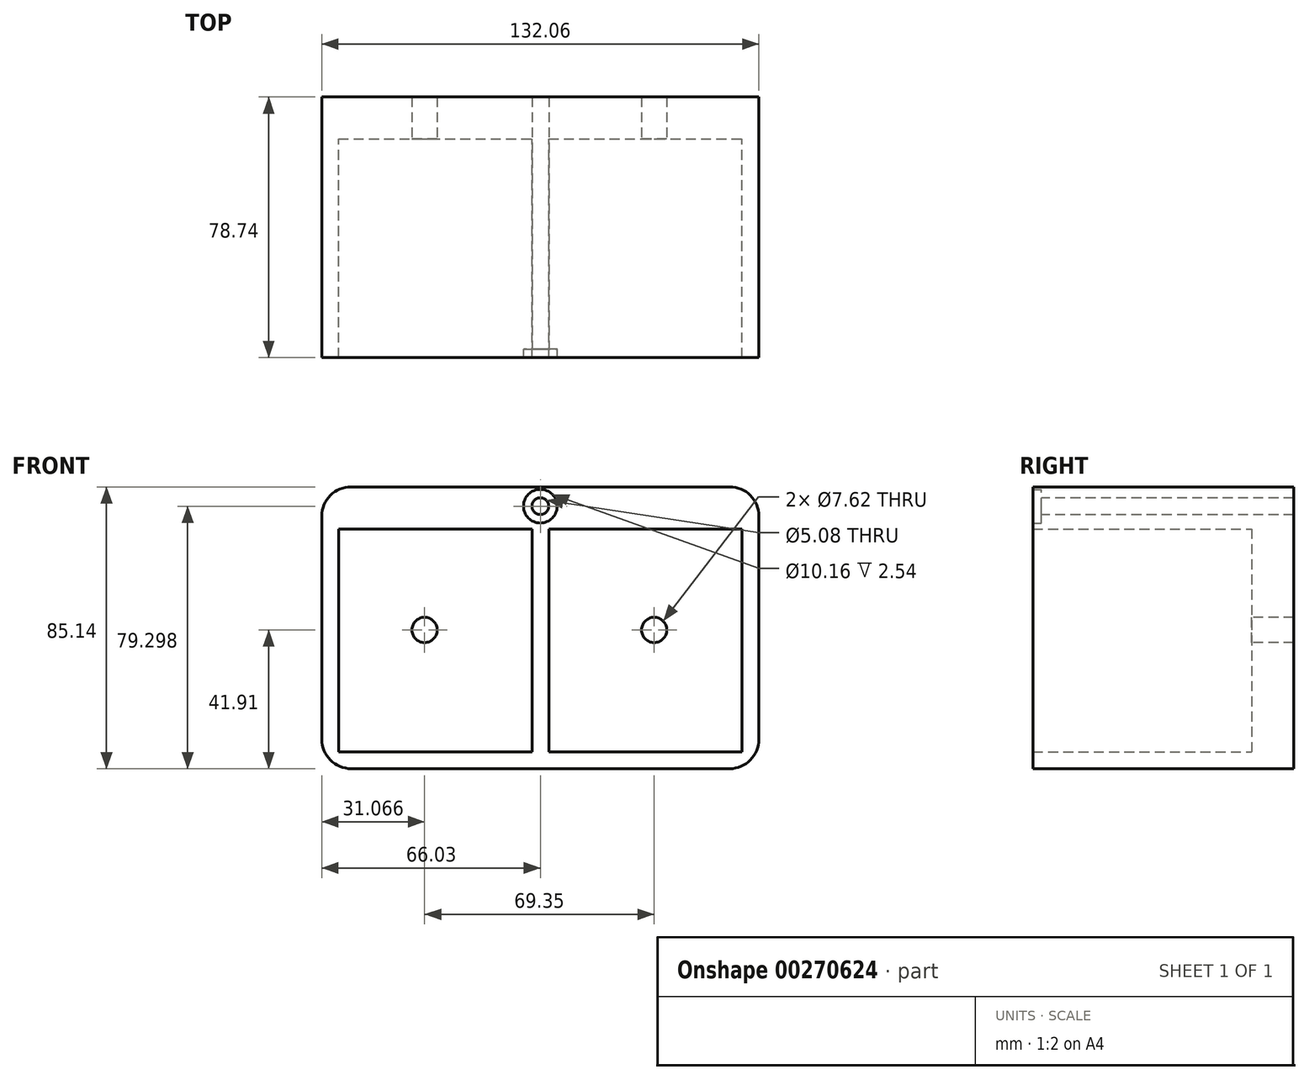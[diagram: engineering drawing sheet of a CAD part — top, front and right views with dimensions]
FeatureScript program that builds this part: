
annotation { "Feature Type Name" : "Feature", "Feature Type Description" : "" }
export const myFeature = defineFeature(function(context is Context, id is Id, definition is map)
    precondition{}
    {
        {
            var Q0;
            Q0=qCreatedBy(makeId("Front.planeOp"),FACE);
            var sketch = newSketch(context, id + "F0", { "sketchPlane" : qUnion([Q0])});
            skLineSegment(sketch, "E0.bottom", {"start": v(66.03, 42.57) * mm, "end": v(-66.03, 42.57) * mm});
            skLineSegment(sketch, "E0.top", {"start": v(66.03, -42.57) * mm, "end": v(-66.03, -42.57) * mm});
            skLineSegment(sketch, "E0.left", {"start": v(66.03, 42.57) * mm, "end": v(66.03, -42.57) * mm});
            skLineSegment(sketch, "E0.right", {"start": v(-66.03, 42.57) * mm, "end": v(-66.03, -42.57) * mm});
            skPoint(sketch, "E0.middle", {"position": v(0, 0) * mm});
            skPoint(sketch, "E1.visualSharp", {"position": v(-66.03, 42.57) * mm});
            skLineSegment(sketch, "E1.filletArc", {"start": v(-66.03, 42.57) * mm, "end": v(-66.03, 42.57) * mm});
            skPoint(sketch, "E2.visualSharp", {"position": v(-66.03, -42.57) * mm});
            skLineSegment(sketch, "E2.filletArc", {"start": v(-66.03, -42.57) * mm, "end": v(-66.03, -42.57) * mm});
            skPoint(sketch, "E3.visualSharp", {"position": v(66.03, -42.57) * mm});
            skLineSegment(sketch, "E3.filletArc", {"start": v(66.03, -42.57) * mm, "end": v(66.03, -42.57) * mm});
            skPoint(sketch, "E4.visualSharp", {"position": v(66.03, 42.57) * mm});
            skLineSegment(sketch, "E4.filletArc", {"start": v(66.03, 42.57) * mm, "end": v(66.03, 42.57) * mm});
            skLineSegment(sketch, "E5.bottom", {"start": v(-2.54, 42.57) * mm, "end": v(2.54, 42.57) * mm});
            skLineSegment(sketch, "E5.top", {"start": v(-2.54, -42.57) * mm, "end": v(2.54, -42.57) * mm});
            skPoint(sketch, "E6.visualSharp", {"position": v(-66.03, 44.93) * mm});
            skPoint(sketch, "E7.visualSharp", {"position": v(58.57, -38.09) * mm});
            skPoint(sketch, "E8.visualSharp", {"position": v(58.57, 37.5) * mm});
            skLineSegment(sketch, "E9.bottom", {"start": v(-60.95, 29.87) * mm, "end": v(-2.54, 29.87) * mm});
            skLineSegment(sketch, "E9.top", {"start": v(-60.95, -37.5) * mm, "end": v(-2.54, -37.5) * mm});
            skLineSegment(sketch, "E9.left", {"start": v(-60.95, 29.87) * mm, "end": v(-60.95, -37.5) * mm});
            skLineSegment(sketch, "E9.right", {"start": v(-2.54, 29.87) * mm, "end": v(-2.54, -37.5) * mm});
            skLineSegment(sketch, "E10.bottom", {"start": v(2.54, 29.87) * mm, "end": v(60.95, 29.87) * mm});
            skLineSegment(sketch, "E10.top", {"start": v(2.54, -37.5) * mm, "end": v(60.95, -37.5) * mm});
            skLineSegment(sketch, "E10.left", {"start": v(2.54, 29.87) * mm, "end": v(2.54, -37.5) * mm});
            skLineSegment(sketch, "E10.right", {"start": v(60.95, 29.87) * mm, "end": v(60.95, -37.5) * mm});
            skSolve(sketch);
        }
        {
            var Q0;
            {var subQ1=sQuery(id+"F0.wireOp",EDGE,"E0.left");Q0=makeQuery(id+"F0.imprint","IMPRINT",FACE,{"disambiguationData":[TD([[makeQuery(id+"F0.imprint","IMPRINT",EDGE,{"derivedFrom":subQ1}),-1.0]])]});}
            extrude(context, id + "F1", {"entities" : qUnion([Q0]), "depth" : 76.2 * mm});
        }
        {
            var Q0;
            Q0=makeQuery(id+"F0.imprint","IMPRINT",FACE,{"disambiguationData":[TD([[makeQuery(id+"F0.imprint","IMPRINT",EDGE,{"derivedFrom":sQuery(id+"F0.wireOp",EDGE,"E9.bottom")}),-1.0]])]});
            var Q1;
            Q1=makeQuery(id+"F0.imprint","IMPRINT",FACE,{"disambiguationData":[TD([[makeQuery(id+"F0.imprint","IMPRINT",EDGE,{"derivedFrom":sQuery(id+"F0.wireOp",EDGE,"E10.bottom")}),-1.0]])]});
            extrude(context, id + "F2", {"entities" : qUnion([Q0, Q1]), "operationType" : NewBodyOperationType.ADD, "depth" : 12.7 * mm});
        }
        {
            var Q0;
            Q0=makeQuery(id+"F1.opExtrude","SWEPT_EDGE",EDGE,{"disambiguationData":[OSD([sQuery(id+"F0.wireOp",EDGE,"E0.bottom"),sQuery(id+"F0.wireOp",EDGE,"E0.left")])]});
            var Q1;
            Q1=makeQuery(id+"F1.opExtrude","SWEPT_EDGE",EDGE,{"disambiguationData":[OSD([sQuery(id+"F0.wireOp",EDGE,"E0.top"),sQuery(id+"F0.wireOp",EDGE,"E0.right")])]});
            var Q2;
            Q2=makeQuery(id+"F1.opExtrude","SWEPT_EDGE",EDGE,{"disambiguationData":[OSD([sQuery(id+"F0.wireOp",EDGE,"E0.top"),sQuery(id+"F0.wireOp",EDGE,"E0.left")])]});
            var Q3;
            Q3=makeQuery(id+"F1.opExtrude","SWEPT_EDGE",EDGE,{"disambiguationData":[OSD([sQuery(id+"F0.wireOp",EDGE,"E0.bottom"),sQuery(id+"F0.wireOp",EDGE,"E0.right")])]});
            fillet(context, id + "F3", {"entities" : qUnion([Q0, Q1, Q2, Q3]), "radius" : 8.9 * mm, "tangentPropagation" : true, "allowEdgeOverflow" : false});
        }
        {
            var Q0;
            Q0=makeQuery(id+"F2.opExtrude","CAP_FACE",FACE,{"disambiguationData":[OSD([sQuery(id+"F0.wireOp",EDGE,"E9.bottom"),sQuery(id+"F0.wireOp",EDGE,"E9.top"),sQuery(id+"F0.wireOp",EDGE,"E9.left"),sQuery(id+"F0.wireOp",EDGE,"E9.right")])],"isStart":false});
            var sketch = newSketch(context, id + "F4", { "sketchPlane" : qUnion([Q0])});
            skCircle(sketch, "E11", {"center": v(-34.96, -0.66) * mm, "radius": 3.8 * mm});
            skCircle(sketch, "E12", {"center": v(34.39, -0.66) * mm, "radius": 3.81 * mm});
            skSolve(sketch);
        }
        {
            var Q0;
            Q0=makeQuery(id+"F4.imprint","IMPRINT",FACE,{"disambiguationData":[TD([[makeQuery(id+"F4.imprint","IMPRINT",EDGE,{"derivedFrom":sQuery(id+"F4.wireOp",EDGE,"E11")}),1.0]])]});
            var Q1;
            Q1=makeQuery(id+"F4.imprint","IMPRINT",FACE,{"disambiguationData":[TD([[makeQuery(id+"F4.imprint","IMPRINT",EDGE,{"derivedFrom":sQuery(id+"F4.wireOp",EDGE,"E12")}),1.0]])]});
            extrude(context, id + "F5", {"entities" : qUnion([Q0, Q1]), "operationType" : NewBodyOperationType.REMOVE, "oppositeDirection" : true, "depth" : 25.4 * mm});
        }
        {
            var Q0;
            Q0=makeQuery(id+"F1.opExtrude","CAP_FACE",FACE,{"disambiguationData":[OSD([sQuery(id+"F0.wireOp",EDGE,"E0.bottom"),sQuery(id+"F0.wireOp",EDGE,"E0.top"),sQuery(id+"F0.wireOp",EDGE,"E0.left"),sQuery(id+"F0.wireOp",EDGE,"E0.right"),sQuery(id+"F0.wireOp",EDGE,"E5.bottom"),sQuery(id+"F0.wireOp",EDGE,"E5.top"),sQuery(id+"F0.wireOp",EDGE,"E9.bottom"),sQuery(id+"F0.wireOp",EDGE,"E9.top"),sQuery(id+"F0.wireOp",EDGE,"E9.left"),sQuery(id+"F0.wireOp",EDGE,"E9.right"),sQuery(id+"F0.wireOp",EDGE,"E10.bottom"),sQuery(id+"F0.wireOp",EDGE,"E10.top"),sQuery(id+"F0.wireOp",EDGE,"E10.left"),sQuery(id+"F0.wireOp",EDGE,"E10.right")])],"isStart":false});
            var sketch = newSketch(context, id + "F6", { "sketchPlane" : qUnion([Q0])});
            skCircle(sketch, "E13", {"center": v(0, 36.73) * mm, "radius": 5.08 * mm});
            skCircle(sketch, "E14", {"center": v(0, 36.73) * mm, "radius": 2.54 * mm});
            skSolve(sketch);
        }
        {
            var Q0;
            Q0=makeQuery(id+"F6.imprint","IMPRINT",FACE,{"disambiguationData":[TD([[makeQuery(id+"F6.imprint","IMPRINT",EDGE,{"derivedFrom":sQuery(id+"F6.wireOp",EDGE,"E14")}),1.0]])]});
            extrude(context, id + "F7", {"entities" : qUnion([Q0]), "operationType" : NewBodyOperationType.REMOVE, "endBound" : BoundingType.THROUGH_ALL, "oppositeDirection" : true, "depth" : 25.4 * mm});
        }
        {
            var Q0;
            Q0=makeQuery(id+"F6.imprint","IMPRINT",FACE,{"disambiguationData":[TD([[makeQuery(id+"F6.imprint","IMPRINT",EDGE,{"derivedFrom":sQuery(id+"F6.wireOp",EDGE,"E13")}),-1.0]])]});
            extrude(context, id + "F8", {"entities" : qUnion([Q0]), "operationType" : NewBodyOperationType.ADD, "depth" : 2.54 * mm});
        }
    });
